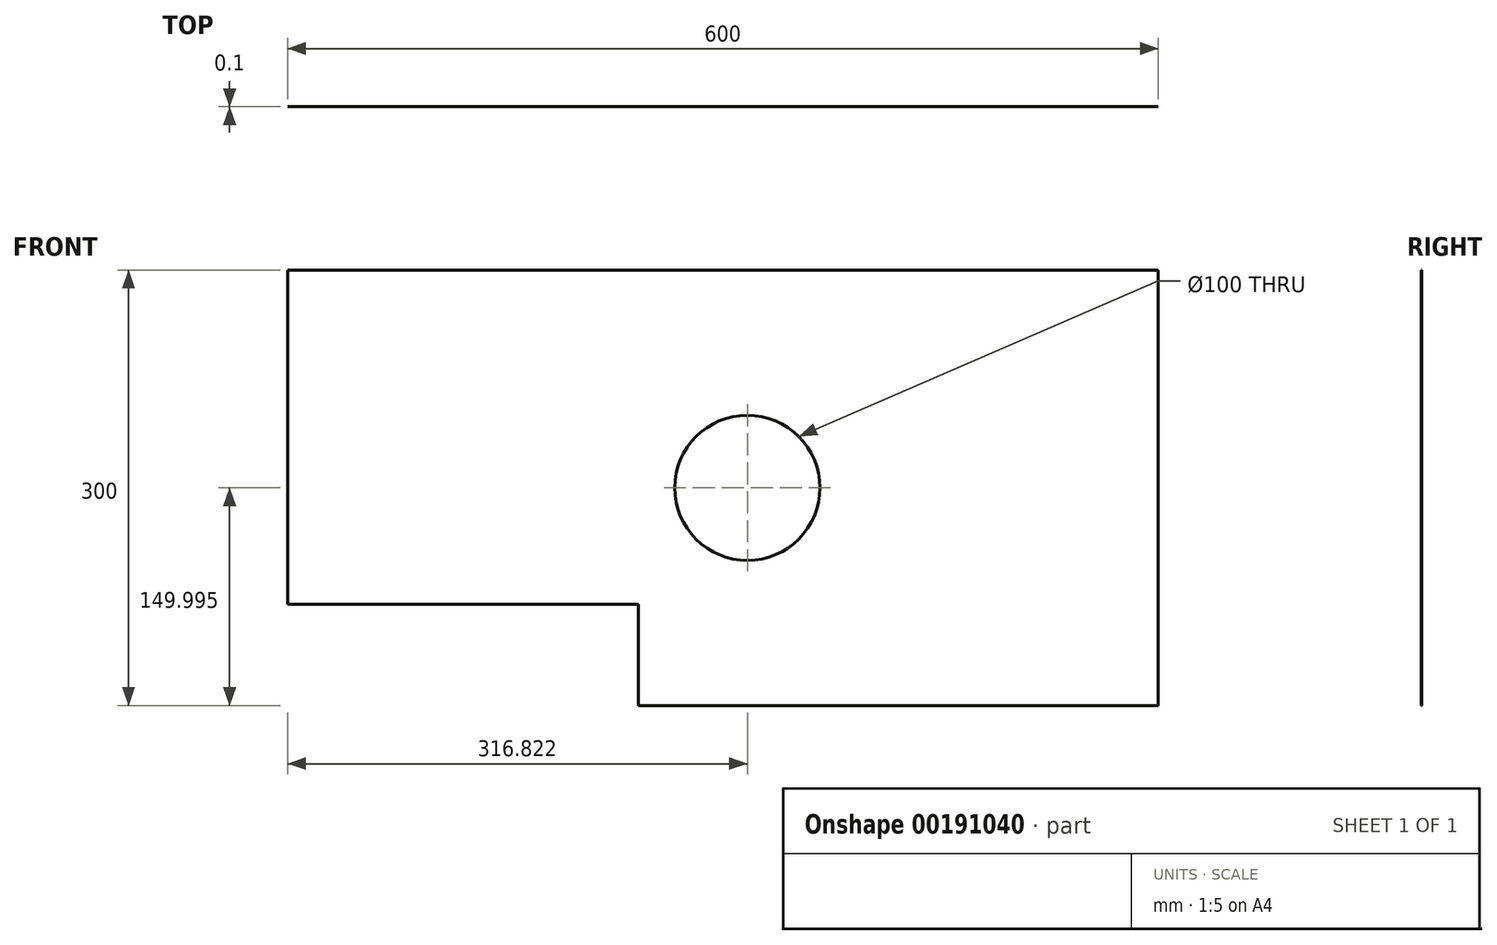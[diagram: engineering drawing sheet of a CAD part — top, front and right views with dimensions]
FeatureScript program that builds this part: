
annotation { "Feature Type Name" : "Feature", "Feature Type Description" : "" }
export const myFeature = defineFeature(function(context is Context, id is Id, definition is map)
    precondition{}
    {
        {
            var Q0;
            Q0=qCreatedBy(makeId("Front.planeOp"),FACE);
            var sketch = newSketch(context, id + "F0", { "sketchPlane" : qUnion([Q0])});
            skLineSegment(sketch, "E0.bottom", {"start": v(-99.5, 250.74) * mm, "end": v(500.5, 250.74) * mm});
            skLineSegment(sketch, "E0.top", {"start": v(142.32, -49.26) * mm, "end": v(500.5, -49.26) * mm});
            skLineSegment(sketch, "E0.left", {"start": v(-99.5, 250.74) * mm, "end": v(-99.5, 20.42) * mm});
            skLineSegment(sketch, "E0.right", {"start": v(500.5, 250.74) * mm, "end": v(500.5, -49.26) * mm});
            skLineSegment(sketch, "E1.top", {"start": v(-99.5, 20.42) * mm, "end": v(142.32, 20.42) * mm});
            skLineSegment(sketch, "E1.right", {"start": v(142.32, -49.26) * mm, "end": v(142.32, 20.42) * mm});
            skCircle(sketch, "E2", {"center": v(217.32, 100.74) * mm, "radius": 50 * mm});
            skSolve(sketch);
        }
        {
            var Q0;
            Q0 = qSketchRegion(id + "F0", true);
            extrude(context, id + "F1", {"entities" : qUnion([Q0]), "depth" : 0.1 * mm});
        }
    });
